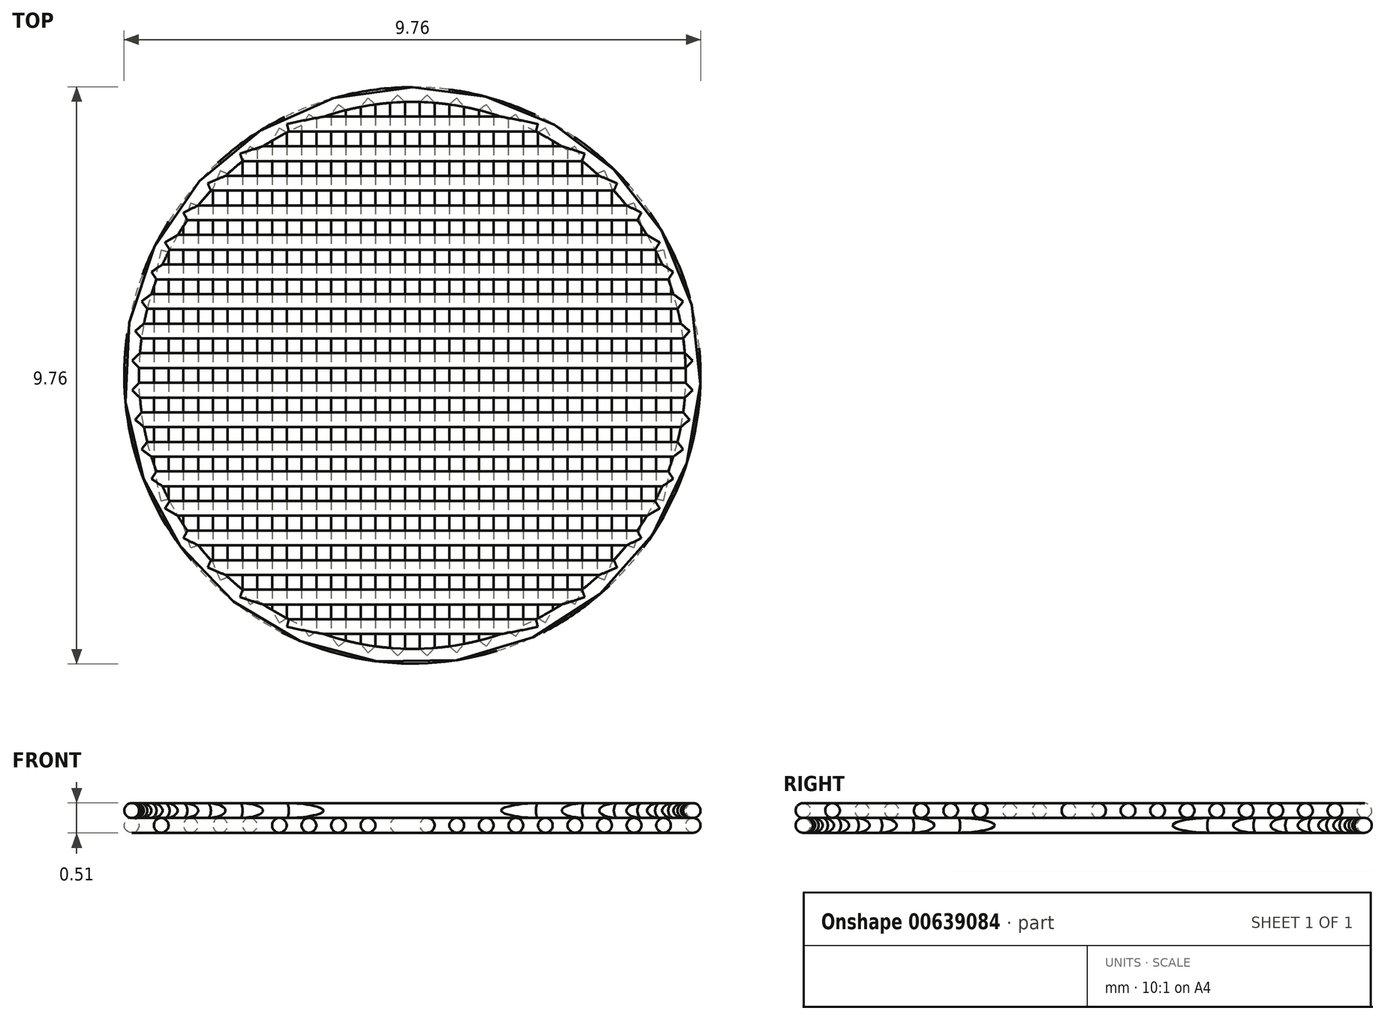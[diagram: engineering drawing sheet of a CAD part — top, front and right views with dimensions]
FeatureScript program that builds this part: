
annotation { "Feature Type Name" : "Feature", "Feature Type Description" : "" }
export const myFeature = defineFeature(function(context is Context, id is Id, definition is map)
    precondition{}
    {
        {
            assignVariable(context, id + "F0", {"name" : "d", "anyValue" : 0.25});
        }
        {
            var Q0;
            Q0=qCreatedBy(makeId("Top.planeOp"),FACE);
            cPlane(context, id + "F1", {"entities" : qUnion([Q0]), "cplaneType" : CPlaneType.OFFSET, "offset" : (getVariable(context, 'd')) * mm, "width" : 150 * mm, "height" : 150 * mm});
        }
        {
            var Q0;
            Q0=qCreatedBy(id+"F1.planeOp",FACE);
            var sketch = newSketch(context, id + "F2", { "sketchPlane" : qUnion([Q0])});
            skLineSegment(sketch, "E0.bottom", {"start": v(5, 5) * mm, "end": v(-5, 5) * mm, "construction": true});
            skLineSegment(sketch, "E0.top", {"start": v(5, -5) * mm, "end": v(-5, -5) * mm, "construction": true});
            skLineSegment(sketch, "E0.left", {"start": v(5, 5) * mm, "end": v(5, -5) * mm, "construction": true});
            skLineSegment(sketch, "E0.right", {"start": v(-5, 5) * mm, "end": v(-5, -5) * mm, "construction": true});
            skPoint(sketch, "E0.middle", {"position": v(0, 0) * mm});
            skCircle(sketch, "E1", {"center": v(0, 0) * mm, "radius": 4.75 * mm});
            skLineSegment(sketch, "E2", {"start": v(-5, 5) * mm, "end": v(-4.75, 5) * mm, "construction": true});
            skLineSegment(sketch, "E3", {"start": v(-4.75, 5) * mm, "end": v(-4.75, -5) * mm, "construction": true});
            skLineSegment(sketch, "E4", {"start": v(-4.75, -5) * mm, "end": v(-5, -5) * mm, "construction": true});
            skLineSegment(sketch, "E5", {"start": v(-4.75, 5) * mm, "end": v(-4.25, 5) * mm, "construction": true});
            skLineSegment(sketch, "E6", {"start": v(-4.25, 5) * mm, "end": v(-4.25, -5) * mm, "construction": true});
            skLineSegment(sketch, "E7", {"start": v(-4.25, -5) * mm, "end": v(-4.75, -5) * mm, "construction": true});
            skLineSegment(sketch, "E8.1.0.0", {"start": v(-3.75, 5) * mm, "end": v(-3.75, -5) * mm, "construction": true});
            skLineSegment(sketch, "E8.1.0.1", {"start": v(-4.25, 5) * mm, "end": v(-3.75, 5) * mm, "construction": true});
            skLineSegment(sketch, "E8.1.0.2", {"start": v(-3.75, -5) * mm, "end": v(-4.25, -5) * mm, "construction": true});
            skLineSegment(sketch, "E8.2.0.0", {"start": v(-3.25, 5) * mm, "end": v(-3.25, -5) * mm, "construction": true});
            skLineSegment(sketch, "E8.2.0.1", {"start": v(-3.75, 5) * mm, "end": v(-3.25, 5) * mm, "construction": true});
            skLineSegment(sketch, "E8.2.0.2", {"start": v(-3.25, -5) * mm, "end": v(-3.75, -5) * mm, "construction": true});
            skLineSegment(sketch, "E8.3.0.0", {"start": v(-2.75, 5) * mm, "end": v(-2.75, -5) * mm, "construction": true});
            skLineSegment(sketch, "E8.3.0.1", {"start": v(-3.25, 5) * mm, "end": v(-2.75, 5) * mm, "construction": true});
            skLineSegment(sketch, "E8.3.0.2", {"start": v(-2.75, -5) * mm, "end": v(-3.25, -5) * mm, "construction": true});
            skLineSegment(sketch, "E8.4.0.0", {"start": v(-2.25, 5) * mm, "end": v(-2.25, -5) * mm, "construction": true});
            skLineSegment(sketch, "E8.4.0.1", {"start": v(-2.75, 5) * mm, "end": v(-2.25, 5) * mm, "construction": true});
            skLineSegment(sketch, "E8.4.0.2", {"start": v(-2.25, -5) * mm, "end": v(-2.75, -5) * mm, "construction": true});
            skLineSegment(sketch, "E8.5.0.0", {"start": v(-1.75, 5) * mm, "end": v(-1.75, -5) * mm, "construction": true});
            skLineSegment(sketch, "E8.5.0.1", {"start": v(-2.25, 5) * mm, "end": v(-1.75, 5) * mm, "construction": true});
            skLineSegment(sketch, "E8.5.0.2", {"start": v(-1.75, -5) * mm, "end": v(-2.25, -5) * mm, "construction": true});
            skLineSegment(sketch, "E8.6.0.0", {"start": v(-1.25, 5) * mm, "end": v(-1.25, -5) * mm, "construction": true});
            skLineSegment(sketch, "E8.6.0.1", {"start": v(-1.75, 5) * mm, "end": v(-1.25, 5) * mm, "construction": true});
            skLineSegment(sketch, "E8.6.0.2", {"start": v(-1.25, -5) * mm, "end": v(-1.75, -5) * mm, "construction": true});
            skLineSegment(sketch, "E8.7.0.0", {"start": v(-0.75, 5) * mm, "end": v(-0.75, -5) * mm, "construction": true});
            skLineSegment(sketch, "E8.7.0.1", {"start": v(-1.25, 5) * mm, "end": v(-0.75, 5) * mm, "construction": true});
            skLineSegment(sketch, "E8.7.0.2", {"start": v(-0.75, -5) * mm, "end": v(-1.25, -5) * mm, "construction": true});
            skLineSegment(sketch, "E8.8.0.0", {"start": v(-0.25, 5) * mm, "end": v(-0.25, -5) * mm, "construction": true});
            skLineSegment(sketch, "E8.8.0.1", {"start": v(-0.75, 5) * mm, "end": v(-0.25, 5) * mm, "construction": true});
            skLineSegment(sketch, "E8.8.0.2", {"start": v(-0.25, -5) * mm, "end": v(-0.75, -5) * mm, "construction": true});
            skLineSegment(sketch, "E8.9.0.0", {"start": v(0.25, 5) * mm, "end": v(0.25, -5) * mm, "construction": true});
            skLineSegment(sketch, "E8.9.0.1", {"start": v(-0.25, 5) * mm, "end": v(0.25, 5) * mm, "construction": true});
            skLineSegment(sketch, "E8.9.0.2", {"start": v(0.25, -5) * mm, "end": v(-0.25, -5) * mm, "construction": true});
            skLineSegment(sketch, "E8.10.0.0", {"start": v(0.75, 5) * mm, "end": v(0.75, -5) * mm, "construction": true});
            skLineSegment(sketch, "E8.10.0.1", {"start": v(0.25, 5) * mm, "end": v(0.75, 5) * mm, "construction": true});
            skLineSegment(sketch, "E8.10.0.2", {"start": v(0.75, -5) * mm, "end": v(0.25, -5) * mm, "construction": true});
            skLineSegment(sketch, "E8.11.0.0", {"start": v(1.25, 5) * mm, "end": v(1.25, -5) * mm, "construction": true});
            skLineSegment(sketch, "E8.11.0.1", {"start": v(0.75, 5) * mm, "end": v(1.25, 5) * mm, "construction": true});
            skLineSegment(sketch, "E8.11.0.2", {"start": v(1.25, -5) * mm, "end": v(0.75, -5) * mm, "construction": true});
            skLineSegment(sketch, "E8.12.0.0", {"start": v(1.75, 5) * mm, "end": v(1.75, -5) * mm, "construction": true});
            skLineSegment(sketch, "E8.12.0.1", {"start": v(1.25, 5) * mm, "end": v(1.75, 5) * mm, "construction": true});
            skLineSegment(sketch, "E8.12.0.2", {"start": v(1.75, -5) * mm, "end": v(1.25, -5) * mm, "construction": true});
            skLineSegment(sketch, "E8.13.0.0", {"start": v(2.25, 5) * mm, "end": v(2.25, -5) * mm, "construction": true});
            skLineSegment(sketch, "E8.13.0.1", {"start": v(1.75, 5) * mm, "end": v(2.25, 5) * mm, "construction": true});
            skLineSegment(sketch, "E8.13.0.2", {"start": v(2.25, -5) * mm, "end": v(1.75, -5) * mm, "construction": true});
            skLineSegment(sketch, "E8.14.0.0", {"start": v(2.75, 5) * mm, "end": v(2.75, -5) * mm, "construction": true});
            skLineSegment(sketch, "E8.14.0.1", {"start": v(2.25, 5) * mm, "end": v(2.75, 5) * mm, "construction": true});
            skLineSegment(sketch, "E8.14.0.2", {"start": v(2.75, -5) * mm, "end": v(2.25, -5) * mm, "construction": true});
            skLineSegment(sketch, "E8.15.0.0", {"start": v(3.25, 5) * mm, "end": v(3.25, -5) * mm, "construction": true});
            skLineSegment(sketch, "E8.15.0.1", {"start": v(2.75, 5) * mm, "end": v(3.25, 5) * mm, "construction": true});
            skLineSegment(sketch, "E8.15.0.2", {"start": v(3.25, -5) * mm, "end": v(2.75, -5) * mm, "construction": true});
            skLineSegment(sketch, "E8.16.0.0", {"start": v(3.75, 5) * mm, "end": v(3.75, -5) * mm, "construction": true});
            skLineSegment(sketch, "E8.16.0.1", {"start": v(3.25, 5) * mm, "end": v(3.75, 5) * mm, "construction": true});
            skLineSegment(sketch, "E8.16.0.2", {"start": v(3.75, -5) * mm, "end": v(3.25, -5) * mm, "construction": true});
            skLineSegment(sketch, "E8.17.0.0", {"start": v(4.25, 5) * mm, "end": v(4.25, -5) * mm, "construction": true});
            skLineSegment(sketch, "E8.17.0.1", {"start": v(3.75, 5) * mm, "end": v(4.25, 5) * mm, "construction": true});
            skLineSegment(sketch, "E8.17.0.2", {"start": v(4.25, -5) * mm, "end": v(3.75, -5) * mm, "construction": true});
            skLineSegment(sketch, "E8.18.0.0", {"start": v(4.75, 5) * mm, "end": v(4.75, -5) * mm, "construction": true});
            skLineSegment(sketch, "E8.18.0.1", {"start": v(4.25, 5) * mm, "end": v(4.75, 5) * mm, "construction": true});
            skLineSegment(sketch, "E8.18.0.2", {"start": v(4.75, -5) * mm, "end": v(4.25, -5) * mm, "construction": true});
            skLineSegment(sketch, "E8.direction1", {"start": v(-4.75, -5) * mm, "end": v(-4.25, -5) * mm, "construction": true});
            skLineSegment(sketch, "E9", {"start": v(4.75, 5) * mm, "end": v(5, 5) * mm, "construction": true});
            skLineSegment(sketch, "E10", {"start": v(4.75, -5) * mm, "end": v(5, -5) * mm, "construction": true});
            skLineSegment(sketch, "E11", {"start": v(-4.25, 2.12) * mm, "end": v(-4.25, -2.12) * mm});
            skLineSegment(sketch, "E12", {"start": v(-3.75, 2.92) * mm, "end": v(-3.75, -2.92) * mm});
            skLineSegment(sketch, "E13", {"start": v(-3.25, 3.46) * mm, "end": v(-3.25, -3.46) * mm});
            skLineSegment(sketch, "E14", {"start": v(-2.75, 3.87) * mm, "end": v(-2.75, -3.87) * mm});
            skLineSegment(sketch, "E15", {"start": v(-2.25, 4.18) * mm, "end": v(-2.25, -4.18) * mm});
            skLineSegment(sketch, "E16", {"start": v(-1.75, 4.42) * mm, "end": v(-1.75, -4.42) * mm});
            skLineSegment(sketch, "E17", {"start": v(-1.25, 4.58) * mm, "end": v(-1.25, -4.58) * mm});
            skLineSegment(sketch, "E18", {"start": v(-0.75, 4.7) * mm, "end": v(-0.75, -4.7) * mm});
            skLineSegment(sketch, "E19", {"start": v(-0.25, 4.74) * mm, "end": v(-0.25, -4.74) * mm});
            skLineSegment(sketch, "E20", {"start": v(0.25, 4.74) * mm, "end": v(0.25, -4.74) * mm});
            skLineSegment(sketch, "E21", {"start": v(0.75, 4.7) * mm, "end": v(0.75, -4.7) * mm});
            skLineSegment(sketch, "E22", {"start": v(1.25, 4.58) * mm, "end": v(1.25, -4.58) * mm});
            skLineSegment(sketch, "E23", {"start": v(1.75, 4.42) * mm, "end": v(1.75, -4.42) * mm});
            skLineSegment(sketch, "E24", {"start": v(2.25, 4.18) * mm, "end": v(2.25, -4.18) * mm});
            skLineSegment(sketch, "E25", {"start": v(2.75, 3.87) * mm, "end": v(2.75, -3.87) * mm});
            skLineSegment(sketch, "E26", {"start": v(3.25, 3.46) * mm, "end": v(3.25, -3.46) * mm});
            skLineSegment(sketch, "E27", {"start": v(3.75, 2.92) * mm, "end": v(3.75, -2.92) * mm});
            skLineSegment(sketch, "E28", {"start": v(4.25, 2.12) * mm, "end": v(4.25, -2.12) * mm});
            skSolve(sketch);
        }
        {
            var Q0;
            Q0=qCreatedBy(makeId("Right.planeOp"),FACE);
            var sketch = newSketch(context, id + "F3", { "sketchPlane" : qUnion([Q0])});
            skCircle(sketch, "E29", {"center": v(-4.75, 0.25) * mm, "radius": 0.13 * mm});
            skSolve(sketch);
        }
        {
            var Q0;
            Q0=makeQuery(id+"F3.imprint","IMPRINT",FACE,{"disambiguationData":[TD([[makeQuery(id+"F3.imprint","IMPRINT",EDGE,{"derivedFrom":sQuery(id+"F3.wireOp",EDGE,"E29")}),1.0]])]});
            var Q1;
            Q1=sQuery(id+"F2.wireOp",EDGE,"E1");
            sweep(context, id + "F4", {"profiles" : qUnion([Q0]), "path" : qUnion([Q1])});
        }
        {
            var Q0;
            Q0=qCreatedBy(makeId("Front.planeOp"),FACE);
            var sketch = newSketch(context, id + "F5", { "sketchPlane" : qUnion([Q0])});
            skCircle(sketch, "E30", {"center": v(-4.25, 0.25) * mm, "radius": 0.12 * mm});
            skCircle(sketch, "E31", {"center": v(-3.75, 0.25) * mm, "radius": 0.12 * mm});
            skCircle(sketch, "E32", {"center": v(-3.25, 0.25) * mm, "radius": 0.12 * mm});
            skCircle(sketch, "E33", {"center": v(-2.75, 0.25) * mm, "radius": 0.12 * mm});
            skCircle(sketch, "E34", {"center": v(-2.25, 0.25) * mm, "radius": 0.12 * mm});
            skCircle(sketch, "E35", {"center": v(-1.75, 0.25) * mm, "radius": 0.12 * mm});
            skCircle(sketch, "E36", {"center": v(-1.25, 0.25) * mm, "radius": 0.12 * mm});
            skCircle(sketch, "E37", {"center": v(-0.75, 0.25) * mm, "radius": 0.12 * mm});
            skCircle(sketch, "E38", {"center": v(-0.25, 0.25) * mm, "radius": 0.12 * mm});
            skCircle(sketch, "E39", {"center": v(0.25, 0.25) * mm, "radius": 0.12 * mm});
            skCircle(sketch, "E40", {"center": v(0.75, 0.25) * mm, "radius": 0.12 * mm});
            skCircle(sketch, "E41", {"center": v(2.25, 0.25) * mm, "radius": 0.12 * mm});
            skCircle(sketch, "E42", {"center": v(1.75, 0.25) * mm, "radius": 0.12 * mm});
            skCircle(sketch, "E43", {"center": v(1.25, 0.25) * mm, "radius": 0.12 * mm});
            skCircle(sketch, "E44", {"center": v(2.75, 0.25) * mm, "radius": 0.12 * mm});
            skCircle(sketch, "E45", {"center": v(3.25, 0.25) * mm, "radius": 0.12 * mm});
            skCircle(sketch, "E46", {"center": v(3.75, 0.25) * mm, "radius": 0.12 * mm});
            skCircle(sketch, "E47", {"center": v(4.25, 0.25) * mm, "radius": 0.12 * mm});
            skSolve(sketch);
        }
        {
            var Q0;
            Q0=makeQuery(id+"F5.imprint","IMPRINT",FACE,{"disambiguationData":[TD([[makeQuery(id+"F5.imprint","IMPRINT",EDGE,{"derivedFrom":sQuery(id+"F5.wireOp",EDGE,"E30")}),1.0]])]});
            var Q1;
            Q1=sQuery(id+"F2.wireOp",EDGE,"E11");
            sweep(context, id + "F6", {"operationType" : NewBodyOperationType.ADD, "profiles" : qUnion([Q0]), "path" : qUnion([Q1])});
        }
        {
            var Q0;
            Q0=makeQuery(id+"F5.imprint","IMPRINT",FACE,{"disambiguationData":[TD([[makeQuery(id+"F5.imprint","IMPRINT",EDGE,{"derivedFrom":sQuery(id+"F5.wireOp",EDGE,"E31")}),1.0]])]});
            var Q1;
            Q1=sQuery(id+"F5.wireOp",EDGE,"E31");
            var Q2;
            Q2=sQuery(id+"F2.wireOp",EDGE,"E12");
            sweep(context, id + "F7", {"operationType" : NewBodyOperationType.ADD, "profiles" : qUnion([Q0]), "surfaceProfiles" : qUnion([Q1]), "path" : qUnion([Q2])});
        }
        {
            var Q0;
            Q0=makeQuery(id+"F5.imprint","IMPRINT",FACE,{"disambiguationData":[TD([[makeQuery(id+"F5.imprint","IMPRINT",EDGE,{"derivedFrom":sQuery(id+"F5.wireOp",EDGE,"E32")}),1.0]])]});
            var Q1;
            Q1=sQuery(id+"F2.wireOp",EDGE,"E13");
            sweep(context, id + "F8", {"operationType" : NewBodyOperationType.ADD, "profiles" : qUnion([Q0]), "path" : qUnion([Q1])});
        }
        {
            var Q0;
            Q0=makeQuery(id+"F5.imprint","IMPRINT",FACE,{"disambiguationData":[TD([[makeQuery(id+"F5.imprint","IMPRINT",EDGE,{"derivedFrom":sQuery(id+"F5.wireOp",EDGE,"E33")}),1.0]])]});
            var Q1;
            Q1=sQuery(id+"F2.wireOp",EDGE,"E14");
            sweep(context, id + "F9", {"operationType" : NewBodyOperationType.ADD, "profiles" : qUnion([Q0]), "path" : qUnion([Q1])});
        }
        {
            var Q0;
            Q0=makeQuery(id+"F5.imprint","IMPRINT",FACE,{"disambiguationData":[TD([[makeQuery(id+"F5.imprint","IMPRINT",EDGE,{"derivedFrom":sQuery(id+"F5.wireOp",EDGE,"E34")}),1.0]])]});
            var Q1;
            Q1=sQuery(id+"F2.wireOp",EDGE,"E15");
            sweep(context, id + "F10", {"operationType" : NewBodyOperationType.ADD, "profiles" : qUnion([Q0]), "path" : qUnion([Q1])});
        }
        {
            var Q0;
            Q0=makeQuery(id+"F5.imprint","IMPRINT",FACE,{"disambiguationData":[TD([[makeQuery(id+"F5.imprint","IMPRINT",EDGE,{"derivedFrom":sQuery(id+"F5.wireOp",EDGE,"E35")}),1.0]])]});
            var Q1;
            Q1=sQuery(id+"F2.wireOp",EDGE,"E16");
            sweep(context, id + "F11", {"operationType" : NewBodyOperationType.ADD, "profiles" : qUnion([Q0]), "path" : qUnion([Q1])});
        }
        {
            var Q0;
            Q0=makeQuery(id+"F5.imprint","IMPRINT",FACE,{"disambiguationData":[TD([[makeQuery(id+"F5.imprint","IMPRINT",EDGE,{"derivedFrom":sQuery(id+"F5.wireOp",EDGE,"E36")}),1.0]])]});
            var Q1;
            Q1=sQuery(id+"F5.wireOp",EDGE,"E36");
            var Q2;
            Q2=sQuery(id+"F2.wireOp",EDGE,"E17");
            sweep(context, id + "F12", {"operationType" : NewBodyOperationType.ADD, "profiles" : qUnion([Q0]), "surfaceProfiles" : qUnion([Q1]), "path" : qUnion([Q2])});
        }
        {
            var Q0;
            Q0=makeQuery(id+"F5.imprint","IMPRINT",FACE,{"disambiguationData":[TD([[makeQuery(id+"F5.imprint","IMPRINT",EDGE,{"derivedFrom":sQuery(id+"F5.wireOp",EDGE,"E37")}),1.0]])]});
            var Q1;
            Q1=sQuery(id+"F2.wireOp",EDGE,"E18");
            sweep(context, id + "F13", {"operationType" : NewBodyOperationType.ADD, "profiles" : qUnion([Q0]), "path" : qUnion([Q1])});
        }
        {
            var Q0;
            Q0=makeQuery(id+"F5.imprint","IMPRINT",FACE,{"disambiguationData":[TD([[makeQuery(id+"F5.imprint","IMPRINT",EDGE,{"derivedFrom":sQuery(id+"F5.wireOp",EDGE,"E38")}),1.0]])]});
            var Q1;
            Q1=sQuery(id+"F2.wireOp",EDGE,"E19");
            sweep(context, id + "F14", {"operationType" : NewBodyOperationType.ADD, "profiles" : qUnion([Q0]), "path" : qUnion([Q1])});
        }
        {
            var Q0;
            Q0=makeQuery(id+"F5.imprint","IMPRINT",FACE,{"disambiguationData":[TD([[makeQuery(id+"F5.imprint","IMPRINT",EDGE,{"derivedFrom":sQuery(id+"F5.wireOp",EDGE,"E39")}),1.0]])]});
            var Q1;
            Q1=sQuery(id+"F2.wireOp",EDGE,"E20");
            sweep(context, id + "F15", {"operationType" : NewBodyOperationType.ADD, "profiles" : qUnion([Q0]), "path" : qUnion([Q1])});
        }
        {
            var Q0;
            Q0=makeQuery(id+"F5.imprint","IMPRINT",FACE,{"disambiguationData":[TD([[makeQuery(id+"F5.imprint","IMPRINT",EDGE,{"derivedFrom":sQuery(id+"F5.wireOp",EDGE,"E40")}),1.0]])]});
            var Q1;
            Q1=sQuery(id+"F2.wireOp",EDGE,"E21");
            sweep(context, id + "F16", {"operationType" : NewBodyOperationType.ADD, "profiles" : qUnion([Q0]), "path" : qUnion([Q1])});
        }
        {
            var Q0;
            Q0=makeQuery(id+"F5.imprint","IMPRINT",FACE,{"disambiguationData":[TD([[makeQuery(id+"F5.imprint","IMPRINT",EDGE,{"derivedFrom":sQuery(id+"F5.wireOp",EDGE,"E43")}),1.0]])]});
            var Q1;
            Q1=sQuery(id+"F2.wireOp",EDGE,"E22");
            sweep(context, id + "F17", {"operationType" : NewBodyOperationType.ADD, "profiles" : qUnion([Q0]), "path" : qUnion([Q1])});
        }
        {
            var Q0;
            Q0=makeQuery(id+"F5.imprint","IMPRINT",FACE,{"disambiguationData":[TD([[makeQuery(id+"F5.imprint","IMPRINT",EDGE,{"derivedFrom":sQuery(id+"F5.wireOp",EDGE,"E42")}),1.0]])]});
            var Q1;
            Q1=sQuery(id+"F2.wireOp",EDGE,"E23");
            sweep(context, id + "F18", {"operationType" : NewBodyOperationType.ADD, "profiles" : qUnion([Q0]), "path" : qUnion([Q1])});
        }
        {
            var Q0;
            Q0=makeQuery(id+"F5.imprint","IMPRINT",FACE,{"disambiguationData":[TD([[makeQuery(id+"F5.imprint","IMPRINT",EDGE,{"derivedFrom":sQuery(id+"F5.wireOp",EDGE,"E41")}),1.0]])]});
            var Q1;
            Q1=sQuery(id+"F2.wireOp",EDGE,"E24");
            sweep(context, id + "F19", {"operationType" : NewBodyOperationType.ADD, "profiles" : qUnion([Q0]), "path" : qUnion([Q1])});
        }
        {
            var Q0;
            Q0=makeQuery(id+"F5.imprint","IMPRINT",FACE,{"disambiguationData":[TD([[makeQuery(id+"F5.imprint","IMPRINT",EDGE,{"derivedFrom":sQuery(id+"F5.wireOp",EDGE,"E44")}),1.0]])]});
            var Q1;
            Q1=sQuery(id+"F2.wireOp",EDGE,"E25");
            sweep(context, id + "F20", {"operationType" : NewBodyOperationType.ADD, "profiles" : qUnion([Q0]), "path" : qUnion([Q1])});
        }
        {
            var Q0;
            Q0=makeQuery(id+"F5.imprint","IMPRINT",FACE,{"disambiguationData":[TD([[makeQuery(id+"F5.imprint","IMPRINT",EDGE,{"derivedFrom":sQuery(id+"F5.wireOp",EDGE,"E45")}),1.0]])]});
            var Q1;
            Q1=sQuery(id+"F2.wireOp",EDGE,"E26");
            sweep(context, id + "F21", {"operationType" : NewBodyOperationType.ADD, "profiles" : qUnion([Q0]), "path" : qUnion([Q1])});
        }
        {
            var Q0;
            Q0=makeQuery(id+"F5.imprint","IMPRINT",FACE,{"disambiguationData":[TD([[makeQuery(id+"F5.imprint","IMPRINT",EDGE,{"derivedFrom":sQuery(id+"F5.wireOp",EDGE,"E46")}),1.0]])]});
            var Q1;
            Q1=sQuery(id+"F2.wireOp",EDGE,"E27");
            sweep(context, id + "F22", {"operationType" : NewBodyOperationType.ADD, "profiles" : qUnion([Q0]), "path" : qUnion([Q1])});
        }
        {
            var Q0;
            Q0=makeQuery(id+"F5.imprint","IMPRINT",FACE,{"disambiguationData":[TD([[makeQuery(id+"F5.imprint","IMPRINT",EDGE,{"derivedFrom":sQuery(id+"F5.wireOp",EDGE,"E47")}),1.0]])]});
            var Q1;
            Q1=sQuery(id+"F2.wireOp",EDGE,"E28");
            sweep(context, id + "F23", {"operationType" : NewBodyOperationType.ADD, "profiles" : qUnion([Q0]), "path" : qUnion([Q1])});
        }
        {
            var Q0;
            Q0=qCreatedBy(id+"F1.planeOp",FACE);
            cPlane(context, id + "F24", {"entities" : qUnion([Q0]), "cplaneType" : CPlaneType.OFFSET, "offset" : (getVariable(context, 'd')) * mm, "width" : 150 * mm, "height" : 150 * mm});
        }
        {
            var Q0;
            Q0=qCreatedBy(id+"F24.planeOp",FACE);
            var sketch = newSketch(context, id + "F25", { "sketchPlane" : qUnion([Q0])});
            skLineSegment(sketch, "E48.bottom", {"start": v(-5, 5) * mm, "end": v(-5, -5) * mm, "construction": true});
            skLineSegment(sketch, "E48.top", {"start": v(5, 5) * mm, "end": v(5, -5) * mm, "construction": true});
            skLineSegment(sketch, "E48.left", {"start": v(-5, 5) * mm, "end": v(5, 5) * mm, "construction": true});
            skLineSegment(sketch, "E48.right", {"start": v(-5, -5) * mm, "end": v(5, -5) * mm, "construction": true});
            skPoint(sketch, "E48.middle", {"position": v(0, 0) * mm});
            skCircle(sketch, "E49", {"center": v(0, 0) * mm, "radius": 4.75 * mm});
            skLineSegment(sketch, "E50", {"start": v(-5, -5) * mm, "end": v(-5, -4.75) * mm, "construction": true});
            skLineSegment(sketch, "E51", {"start": v(-5, -4.75) * mm, "end": v(5, -4.75) * mm, "construction": true});
            skLineSegment(sketch, "E52", {"start": v(5, -4.75) * mm, "end": v(5, -5) * mm, "construction": true});
            skLineSegment(sketch, "E53", {"start": v(-5, -4.75) * mm, "end": v(-5, -4.25) * mm, "construction": true});
            skLineSegment(sketch, "E54", {"start": v(-5, -4.25) * mm, "end": v(5, -4.25) * mm, "construction": true});
            skLineSegment(sketch, "E55", {"start": v(5, -4.25) * mm, "end": v(5, -4.75) * mm, "construction": true});
            skLineSegment(sketch, "E56.1.0.0", {"start": v(-5, -3.75) * mm, "end": v(5, -3.75) * mm, "construction": true});
            skLineSegment(sketch, "E56.1.0.1", {"start": v(-5, -4.25) * mm, "end": v(-5, -3.75) * mm, "construction": true});
            skLineSegment(sketch, "E56.1.0.2", {"start": v(5, -3.75) * mm, "end": v(5, -4.25) * mm, "construction": true});
            skLineSegment(sketch, "E56.2.0.0", {"start": v(-5, -3.25) * mm, "end": v(5, -3.25) * mm, "construction": true});
            skLineSegment(sketch, "E56.2.0.1", {"start": v(-5, -3.75) * mm, "end": v(-5, -3.25) * mm, "construction": true});
            skLineSegment(sketch, "E56.2.0.2", {"start": v(5, -3.25) * mm, "end": v(5, -3.75) * mm, "construction": true});
            skLineSegment(sketch, "E56.3.0.0", {"start": v(-5, -2.75) * mm, "end": v(5, -2.75) * mm, "construction": true});
            skLineSegment(sketch, "E56.3.0.1", {"start": v(-5, -3.25) * mm, "end": v(-5, -2.75) * mm, "construction": true});
            skLineSegment(sketch, "E56.3.0.2", {"start": v(5, -2.75) * mm, "end": v(5, -3.25) * mm, "construction": true});
            skLineSegment(sketch, "E56.4.0.0", {"start": v(-5, -2.25) * mm, "end": v(5, -2.25) * mm, "construction": true});
            skLineSegment(sketch, "E56.4.0.1", {"start": v(-5, -2.75) * mm, "end": v(-5, -2.25) * mm, "construction": true});
            skLineSegment(sketch, "E56.4.0.2", {"start": v(5, -2.25) * mm, "end": v(5, -2.75) * mm, "construction": true});
            skLineSegment(sketch, "E56.5.0.0", {"start": v(-5, -1.75) * mm, "end": v(5, -1.75) * mm, "construction": true});
            skLineSegment(sketch, "E56.5.0.1", {"start": v(-5, -2.25) * mm, "end": v(-5, -1.75) * mm, "construction": true});
            skLineSegment(sketch, "E56.5.0.2", {"start": v(5, -1.75) * mm, "end": v(5, -2.25) * mm, "construction": true});
            skLineSegment(sketch, "E56.6.0.0", {"start": v(-5, -1.25) * mm, "end": v(5, -1.25) * mm, "construction": true});
            skLineSegment(sketch, "E56.6.0.1", {"start": v(-5, -1.75) * mm, "end": v(-5, -1.25) * mm, "construction": true});
            skLineSegment(sketch, "E56.6.0.2", {"start": v(5, -1.25) * mm, "end": v(5, -1.75) * mm, "construction": true});
            skLineSegment(sketch, "E56.7.0.0", {"start": v(-5, -0.75) * mm, "end": v(5, -0.75) * mm, "construction": true});
            skLineSegment(sketch, "E56.7.0.1", {"start": v(-5, -1.25) * mm, "end": v(-5, -0.75) * mm, "construction": true});
            skLineSegment(sketch, "E56.7.0.2", {"start": v(5, -0.75) * mm, "end": v(5, -1.25) * mm, "construction": true});
            skLineSegment(sketch, "E56.8.0.0", {"start": v(-5, -0.25) * mm, "end": v(5, -0.25) * mm, "construction": true});
            skLineSegment(sketch, "E56.8.0.1", {"start": v(-5, -0.75) * mm, "end": v(-5, -0.25) * mm, "construction": true});
            skLineSegment(sketch, "E56.8.0.2", {"start": v(5, -0.25) * mm, "end": v(5, -0.75) * mm, "construction": true});
            skLineSegment(sketch, "E56.9.0.0", {"start": v(-5, 0.25) * mm, "end": v(5, 0.25) * mm, "construction": true});
            skLineSegment(sketch, "E56.9.0.1", {"start": v(-5, -0.25) * mm, "end": v(-5, 0.25) * mm, "construction": true});
            skLineSegment(sketch, "E56.9.0.2", {"start": v(5, 0.25) * mm, "end": v(5, -0.25) * mm, "construction": true});
            skLineSegment(sketch, "E56.10.0.0", {"start": v(-5, 0.75) * mm, "end": v(5, 0.75) * mm, "construction": true});
            skLineSegment(sketch, "E56.10.0.1", {"start": v(-5, 0.25) * mm, "end": v(-5, 0.75) * mm, "construction": true});
            skLineSegment(sketch, "E56.10.0.2", {"start": v(5, 0.75) * mm, "end": v(5, 0.25) * mm, "construction": true});
            skLineSegment(sketch, "E56.11.0.0", {"start": v(-5, 1.25) * mm, "end": v(5, 1.25) * mm, "construction": true});
            skLineSegment(sketch, "E56.11.0.1", {"start": v(-5, 0.75) * mm, "end": v(-5, 1.25) * mm, "construction": true});
            skLineSegment(sketch, "E56.11.0.2", {"start": v(5, 1.25) * mm, "end": v(5, 0.75) * mm, "construction": true});
            skLineSegment(sketch, "E56.12.0.0", {"start": v(-5, 1.75) * mm, "end": v(5, 1.75) * mm, "construction": true});
            skLineSegment(sketch, "E56.12.0.1", {"start": v(-5, 1.25) * mm, "end": v(-5, 1.75) * mm, "construction": true});
            skLineSegment(sketch, "E56.12.0.2", {"start": v(5, 1.75) * mm, "end": v(5, 1.25) * mm, "construction": true});
            skLineSegment(sketch, "E56.13.0.0", {"start": v(-5, 2.25) * mm, "end": v(5, 2.25) * mm, "construction": true});
            skLineSegment(sketch, "E56.13.0.1", {"start": v(-5, 1.75) * mm, "end": v(-5, 2.25) * mm, "construction": true});
            skLineSegment(sketch, "E56.13.0.2", {"start": v(5, 2.25) * mm, "end": v(5, 1.75) * mm, "construction": true});
            skLineSegment(sketch, "E56.14.0.0", {"start": v(-5, 2.75) * mm, "end": v(5, 2.75) * mm, "construction": true});
            skLineSegment(sketch, "E56.14.0.1", {"start": v(-5, 2.25) * mm, "end": v(-5, 2.75) * mm, "construction": true});
            skLineSegment(sketch, "E56.14.0.2", {"start": v(5, 2.75) * mm, "end": v(5, 2.25) * mm, "construction": true});
            skLineSegment(sketch, "E56.15.0.0", {"start": v(-5, 3.25) * mm, "end": v(5, 3.25) * mm, "construction": true});
            skLineSegment(sketch, "E56.15.0.1", {"start": v(-5, 2.75) * mm, "end": v(-5, 3.25) * mm, "construction": true});
            skLineSegment(sketch, "E56.15.0.2", {"start": v(5, 3.25) * mm, "end": v(5, 2.75) * mm, "construction": true});
            skLineSegment(sketch, "E56.16.0.0", {"start": v(-5, 3.75) * mm, "end": v(5, 3.75) * mm, "construction": true});
            skLineSegment(sketch, "E56.16.0.1", {"start": v(-5, 3.25) * mm, "end": v(-5, 3.75) * mm, "construction": true});
            skLineSegment(sketch, "E56.16.0.2", {"start": v(5, 3.75) * mm, "end": v(5, 3.25) * mm, "construction": true});
            skLineSegment(sketch, "E56.17.0.0", {"start": v(-5, 4.25) * mm, "end": v(5, 4.25) * mm, "construction": true});
            skLineSegment(sketch, "E56.17.0.1", {"start": v(-5, 3.75) * mm, "end": v(-5, 4.25) * mm, "construction": true});
            skLineSegment(sketch, "E56.17.0.2", {"start": v(5, 4.25) * mm, "end": v(5, 3.75) * mm, "construction": true});
            skLineSegment(sketch, "E56.18.0.0", {"start": v(-5, 4.75) * mm, "end": v(5, 4.75) * mm, "construction": true});
            skLineSegment(sketch, "E56.18.0.1", {"start": v(-5, 4.25) * mm, "end": v(-5, 4.75) * mm, "construction": true});
            skLineSegment(sketch, "E56.18.0.2", {"start": v(5, 4.75) * mm, "end": v(5, 4.25) * mm, "construction": true});
            skLineSegment(sketch, "E56.direction1", {"start": v(5, -4.75) * mm, "end": v(5, -4.25) * mm, "construction": true});
            skLineSegment(sketch, "E57", {"start": v(-5, 4.75) * mm, "end": v(-5, 5) * mm, "construction": true});
            skLineSegment(sketch, "E58", {"start": v(5, 4.75) * mm, "end": v(5, 5) * mm, "construction": true});
            skLineSegment(sketch, "E59", {"start": v(-2.12, -4.25) * mm, "end": v(2.12, -4.25) * mm});
            skLineSegment(sketch, "E60", {"start": v(-2.92, -3.75) * mm, "end": v(2.92, -3.75) * mm});
            skLineSegment(sketch, "E61", {"start": v(-3.46, -3.25) * mm, "end": v(3.46, -3.25) * mm});
            skLineSegment(sketch, "E62", {"start": v(-3.87, -2.75) * mm, "end": v(3.87, -2.75) * mm});
            skLineSegment(sketch, "E63", {"start": v(-4.18, -2.25) * mm, "end": v(4.18, -2.25) * mm});
            skLineSegment(sketch, "E64", {"start": v(-4.42, -1.75) * mm, "end": v(4.42, -1.75) * mm});
            skLineSegment(sketch, "E65", {"start": v(-4.58, -1.25) * mm, "end": v(4.58, -1.25) * mm});
            skLineSegment(sketch, "E66", {"start": v(-4.7, -0.75) * mm, "end": v(4.7, -0.75) * mm});
            skLineSegment(sketch, "E67", {"start": v(-4.74, -0.25) * mm, "end": v(4.74, -0.25) * mm});
            skLineSegment(sketch, "E68", {"start": v(-4.74, 0.25) * mm, "end": v(4.74, 0.25) * mm});
            skLineSegment(sketch, "E69", {"start": v(-4.7, 0.75) * mm, "end": v(4.7, 0.75) * mm});
            skLineSegment(sketch, "E70", {"start": v(-4.58, 1.25) * mm, "end": v(4.58, 1.25) * mm});
            skLineSegment(sketch, "E71", {"start": v(-4.42, 1.75) * mm, "end": v(4.42, 1.75) * mm});
            skLineSegment(sketch, "E72", {"start": v(-4.18, 2.25) * mm, "end": v(4.18, 2.25) * mm});
            skLineSegment(sketch, "E73", {"start": v(-3.87, 2.75) * mm, "end": v(3.87, 2.75) * mm});
            skLineSegment(sketch, "E74", {"start": v(-3.46, 3.25) * mm, "end": v(3.46, 3.25) * mm});
            skLineSegment(sketch, "E75", {"start": v(-2.92, 3.75) * mm, "end": v(2.92, 3.75) * mm});
            skLineSegment(sketch, "E76", {"start": v(-2.12, 4.25) * mm, "end": v(2.12, 4.25) * mm});
            skSolve(sketch);
        }
        {
            var Q0;
            Q0=qCreatedBy(makeId("Front.planeOp"),FACE);
            var sketch = newSketch(context, id + "F26", { "sketchPlane" : qUnion([Q0])});
            skCircle(sketch, "E77", {"center": v(-4.75, 0.5) * mm, "radius": 0.13 * mm});
            skSolve(sketch);
        }
        {
            var Q0;
            Q0=makeQuery(id+"F26.imprint","IMPRINT",FACE,{"disambiguationData":[TD([[makeQuery(id+"F26.imprint","IMPRINT",EDGE,{"derivedFrom":sQuery(id+"F26.wireOp",EDGE,"E77")}),1.0]])]});
            var Q1;
            Q1=sQuery(id+"F26.wireOp",EDGE,"E77");
            var Q2;
            Q2=sQuery(id+"F25.wireOp",EDGE,"E49");
            sweep(context, id + "F27", {"profiles" : qUnion([Q0]), "surfaceProfiles" : qUnion([Q1]), "path" : qUnion([Q2])});
        }
        {
            var Q0;
            Q0=qCreatedBy(makeId("Right.planeOp"),FACE);
            var sketch = newSketch(context, id + "F28", { "sketchPlane" : qUnion([Q0])});
            skCircle(sketch, "E78", {"center": v(-4.25, 0.5) * mm, "radius": 0.12 * mm});
            skCircle(sketch, "E79", {"center": v(-3.75, 0.5) * mm, "radius": 0.12 * mm});
            skCircle(sketch, "E80", {"center": v(-3.25, 0.5) * mm, "radius": 0.12 * mm});
            skCircle(sketch, "E81", {"center": v(-2.75, 0.5) * mm, "radius": 0.12 * mm});
            skCircle(sketch, "E82", {"center": v(-2.25, 0.5) * mm, "radius": 0.12 * mm});
            skCircle(sketch, "E83", {"center": v(-1.75, 0.5) * mm, "radius": 0.12 * mm});
            skCircle(sketch, "E84", {"center": v(-1.25, 0.5) * mm, "radius": 0.12 * mm});
            skCircle(sketch, "E85", {"center": v(-0.75, 0.5) * mm, "radius": 0.12 * mm});
            skCircle(sketch, "E86", {"center": v(0.25, 0.5) * mm, "radius": 0.12 * mm});
            skCircle(sketch, "E87", {"center": v(-0.25, 0.5) * mm, "radius": 0.12 * mm});
            skCircle(sketch, "E88", {"center": v(0.75, 0.5) * mm, "radius": 0.12 * mm});
            skCircle(sketch, "E89", {"center": v(1.25, 0.5) * mm, "radius": 0.12 * mm});
            skCircle(sketch, "E90", {"center": v(2.75, 0.5) * mm, "radius": 0.12 * mm});
            skCircle(sketch, "E91", {"center": v(3.75, 0.5) * mm, "radius": 0.12 * mm});
            skCircle(sketch, "E92", {"center": v(3.25, 0.5) * mm, "radius": 0.12 * mm});
            skCircle(sketch, "E93", {"center": v(2.25, 0.5) * mm, "radius": 0.12 * mm});
            skCircle(sketch, "E94", {"center": v(1.75, 0.5) * mm, "radius": 0.12 * mm});
            skCircle(sketch, "E95", {"center": v(4.25, 0.5) * mm, "radius": 0.12 * mm});
            skSolve(sketch);
        }
        {
            var Q0;
            Q0=makeQuery(id+"F28.imprint","IMPRINT",FACE,{"disambiguationData":[TD([[makeQuery(id+"F28.imprint","IMPRINT",EDGE,{"derivedFrom":sQuery(id+"F28.wireOp",EDGE,"E78")}),1.0]])]});
            var Q1;
            Q1=sQuery(id+"F25.wireOp",EDGE,"E59");
            sweep(context, id + "F29", {"operationType" : NewBodyOperationType.ADD, "profiles" : qUnion([Q0]), "path" : qUnion([Q1])});
        }
        {
            var Q0;
            Q0=makeQuery(id+"F28.imprint","IMPRINT",FACE,{"disambiguationData":[TD([[makeQuery(id+"F28.imprint","IMPRINT",EDGE,{"derivedFrom":sQuery(id+"F28.wireOp",EDGE,"E79")}),1.0]])]});
            var Q1;
            Q1=sQuery(id+"F25.wireOp",EDGE,"E60");
            sweep(context, id + "F30", {"operationType" : NewBodyOperationType.ADD, "profiles" : qUnion([Q0]), "path" : qUnion([Q1])});
        }
        {
            var Q0;
            Q0=makeQuery(id+"F28.imprint","IMPRINT",FACE,{"disambiguationData":[TD([[makeQuery(id+"F28.imprint","IMPRINT",EDGE,{"derivedFrom":sQuery(id+"F28.wireOp",EDGE,"E80")}),1.0]])]});
            var Q1;
            Q1=sQuery(id+"F25.wireOp",EDGE,"E61");
            sweep(context, id + "F31", {"operationType" : NewBodyOperationType.ADD, "profiles" : qUnion([Q0]), "path" : qUnion([Q1])});
        }
        {
            var Q0;
            Q0=makeQuery(id+"F28.imprint","IMPRINT",FACE,{"disambiguationData":[TD([[makeQuery(id+"F28.imprint","IMPRINT",EDGE,{"derivedFrom":sQuery(id+"F28.wireOp",EDGE,"E81")}),1.0]])]});
            var Q1;
            Q1=sQuery(id+"F25.wireOp",EDGE,"E62");
            sweep(context, id + "F32", {"operationType" : NewBodyOperationType.ADD, "profiles" : qUnion([Q0]), "path" : qUnion([Q1])});
        }
        {
            var Q0;
            Q0=makeQuery(id+"F28.imprint","IMPRINT",FACE,{"disambiguationData":[TD([[makeQuery(id+"F28.imprint","IMPRINT",EDGE,{"derivedFrom":sQuery(id+"F28.wireOp",EDGE,"E82")}),1.0]])]});
            var Q1;
            Q1=sQuery(id+"F25.wireOp",EDGE,"E63");
            sweep(context, id + "F33", {"operationType" : NewBodyOperationType.ADD, "profiles" : qUnion([Q0]), "path" : qUnion([Q1])});
        }
        {
            var Q0;
            Q0=makeQuery(id+"F28.imprint","IMPRINT",FACE,{"disambiguationData":[TD([[makeQuery(id+"F28.imprint","IMPRINT",EDGE,{"derivedFrom":sQuery(id+"F28.wireOp",EDGE,"E83")}),1.0]])]});
            var Q1;
            Q1=sQuery(id+"F25.wireOp",EDGE,"E64");
            sweep(context, id + "F34", {"operationType" : NewBodyOperationType.ADD, "profiles" : qUnion([Q0]), "path" : qUnion([Q1])});
        }
        {
            var Q0;
            Q0=makeQuery(id+"F28.imprint","IMPRINT",FACE,{"disambiguationData":[TD([[makeQuery(id+"F28.imprint","IMPRINT",EDGE,{"derivedFrom":sQuery(id+"F28.wireOp",EDGE,"E84")}),1.0]])]});
            var Q1;
            Q1=sQuery(id+"F25.wireOp",EDGE,"E65");
            sweep(context, id + "F35", {"operationType" : NewBodyOperationType.ADD, "profiles" : qUnion([Q0]), "path" : qUnion([Q1])});
        }
        {
            var Q0;
            Q0=makeQuery(id+"F28.imprint","IMPRINT",FACE,{"disambiguationData":[TD([[makeQuery(id+"F28.imprint","IMPRINT",EDGE,{"derivedFrom":sQuery(id+"F28.wireOp",EDGE,"E85")}),1.0]])]});
            var Q1;
            Q1=sQuery(id+"F25.wireOp",EDGE,"E66");
            sweep(context, id + "F36", {"operationType" : NewBodyOperationType.ADD, "profiles" : qUnion([Q0]), "path" : qUnion([Q1])});
        }
        {
            var Q0;
            Q0=makeQuery(id+"F28.imprint","IMPRINT",FACE,{"disambiguationData":[TD([[makeQuery(id+"F28.imprint","IMPRINT",EDGE,{"derivedFrom":sQuery(id+"F28.wireOp",EDGE,"E87")}),1.0]])]});
            var Q1;
            Q1=sQuery(id+"F25.wireOp",EDGE,"E67");
            sweep(context, id + "F37", {"operationType" : NewBodyOperationType.ADD, "profiles" : qUnion([Q0]), "path" : qUnion([Q1])});
        }
        {
            var Q0;
            Q0=makeQuery(id+"F28.imprint","IMPRINT",FACE,{"disambiguationData":[TD([[makeQuery(id+"F28.imprint","IMPRINT",EDGE,{"derivedFrom":sQuery(id+"F28.wireOp",EDGE,"E86")}),1.0]])]});
            var Q1;
            Q1=sQuery(id+"F25.wireOp",EDGE,"E68");
            sweep(context, id + "F38", {"operationType" : NewBodyOperationType.ADD, "profiles" : qUnion([Q0]), "path" : qUnion([Q1])});
        }
        {
            var Q0;
            Q0=makeQuery(id+"F28.imprint","IMPRINT",FACE,{"disambiguationData":[TD([[makeQuery(id+"F28.imprint","IMPRINT",EDGE,{"derivedFrom":sQuery(id+"F28.wireOp",EDGE,"E88")}),1.0]])]});
            var Q1;
            Q1=sQuery(id+"F25.wireOp",EDGE,"E69");
            sweep(context, id + "F39", {"operationType" : NewBodyOperationType.ADD, "profiles" : qUnion([Q0]), "path" : qUnion([Q1])});
        }
        {
            var Q0;
            Q0=makeQuery(id+"F28.imprint","IMPRINT",FACE,{"disambiguationData":[TD([[makeQuery(id+"F28.imprint","IMPRINT",EDGE,{"derivedFrom":sQuery(id+"F28.wireOp",EDGE,"E89")}),1.0]])]});
            var Q1;
            Q1=sQuery(id+"F25.wireOp",EDGE,"E70");
            sweep(context, id + "F40", {"operationType" : NewBodyOperationType.ADD, "profiles" : qUnion([Q0]), "path" : qUnion([Q1])});
        }
        {
            var Q0;
            Q0=makeQuery(id+"F28.imprint","IMPRINT",FACE,{"disambiguationData":[TD([[makeQuery(id+"F28.imprint","IMPRINT",EDGE,{"derivedFrom":sQuery(id+"F28.wireOp",EDGE,"E94")}),1.0]])]});
            var Q1;
            Q1=sQuery(id+"F25.wireOp",EDGE,"E71");
            sweep(context, id + "F41", {"operationType" : NewBodyOperationType.ADD, "profiles" : qUnion([Q0]), "path" : qUnion([Q1])});
        }
        {
            var Q0;
            Q0=makeQuery(id+"F28.imprint","IMPRINT",FACE,{"disambiguationData":[TD([[makeQuery(id+"F28.imprint","IMPRINT",EDGE,{"derivedFrom":sQuery(id+"F28.wireOp",EDGE,"E93")}),1.0]])]});
            var Q1;
            Q1=sQuery(id+"F25.wireOp",EDGE,"E72");
            sweep(context, id + "F42", {"operationType" : NewBodyOperationType.ADD, "profiles" : qUnion([Q0]), "path" : qUnion([Q1])});
        }
        {
            var Q0;
            Q0=makeQuery(id+"F28.imprint","IMPRINT",FACE,{"disambiguationData":[TD([[makeQuery(id+"F28.imprint","IMPRINT",EDGE,{"derivedFrom":sQuery(id+"F28.wireOp",EDGE,"E90")}),1.0]])]});
            var Q1;
            Q1=sQuery(id+"F25.wireOp",EDGE,"E73");
            sweep(context, id + "F43", {"operationType" : NewBodyOperationType.ADD, "profiles" : qUnion([Q0]), "path" : qUnion([Q1])});
        }
        {
            var Q0;
            Q0=makeQuery(id+"F28.imprint","IMPRINT",FACE,{"disambiguationData":[TD([[makeQuery(id+"F28.imprint","IMPRINT",EDGE,{"derivedFrom":sQuery(id+"F28.wireOp",EDGE,"E92")}),1.0]])]});
            var Q1;
            Q1=sQuery(id+"F25.wireOp",EDGE,"E74");
            sweep(context, id + "F44", {"operationType" : NewBodyOperationType.ADD, "profiles" : qUnion([Q0]), "path" : qUnion([Q1])});
        }
        {
            var Q0;
            Q0=makeQuery(id+"F28.imprint","IMPRINT",FACE,{"disambiguationData":[TD([[makeQuery(id+"F28.imprint","IMPRINT",EDGE,{"derivedFrom":sQuery(id+"F28.wireOp",EDGE,"E91")}),1.0]])]});
            var Q1;
            Q1=sQuery(id+"F25.wireOp",EDGE,"E75");
            sweep(context, id + "F45", {"operationType" : NewBodyOperationType.ADD, "profiles" : qUnion([Q0]), "path" : qUnion([Q1])});
        }
        {
            var Q0;
            Q0=makeQuery(id+"F28.imprint","IMPRINT",FACE,{"disambiguationData":[TD([[makeQuery(id+"F28.imprint","IMPRINT",EDGE,{"derivedFrom":sQuery(id+"F28.wireOp",EDGE,"E95")}),1.0]])]});
            var Q1;
            Q1=sQuery(id+"F25.wireOp",EDGE,"E76");
            sweep(context, id + "F46", {"operationType" : NewBodyOperationType.ADD, "profiles" : qUnion([Q0]), "path" : qUnion([Q1])});
        }
    });
